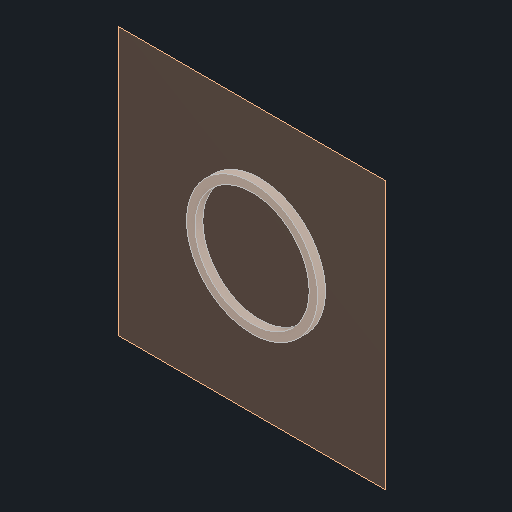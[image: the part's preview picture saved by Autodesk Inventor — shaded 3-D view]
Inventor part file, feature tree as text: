
AUTODESK INVENTOR PART (.ipt)
format: ipt  version: 2023.2 (Build 272271000, 271)  size: 115,712 bytes
history: native  units: mm
features: other x3, plane x1, extrude x1, sketch x1
ambient origin geometry x8: Origin, YZ Plane, XZ Plane, XY Plane, X Axis, Y Axis, Z Axis, Center Point
bodies: Solid1 (feature_tree)
feature tree (6):
  plane  "Work Plane1"
  extrude  "Extrusion1"  Depth=2.8mm
  sketch  "Sketch1"  dims[d0=46.8mm d1=40.8mm d2=2.8mm d3=0.0mm]
  parser-record x1  (decoder bookkeeping rows leaked as tree rows — omitted from the tree; the rows remain in map.json)
  other  "turret_assembly.iam"
  other  "horizontal_lower_bearing_holder:1"
note: 1 file-system path scrubbed to <path> (originals preserved in map.json)
